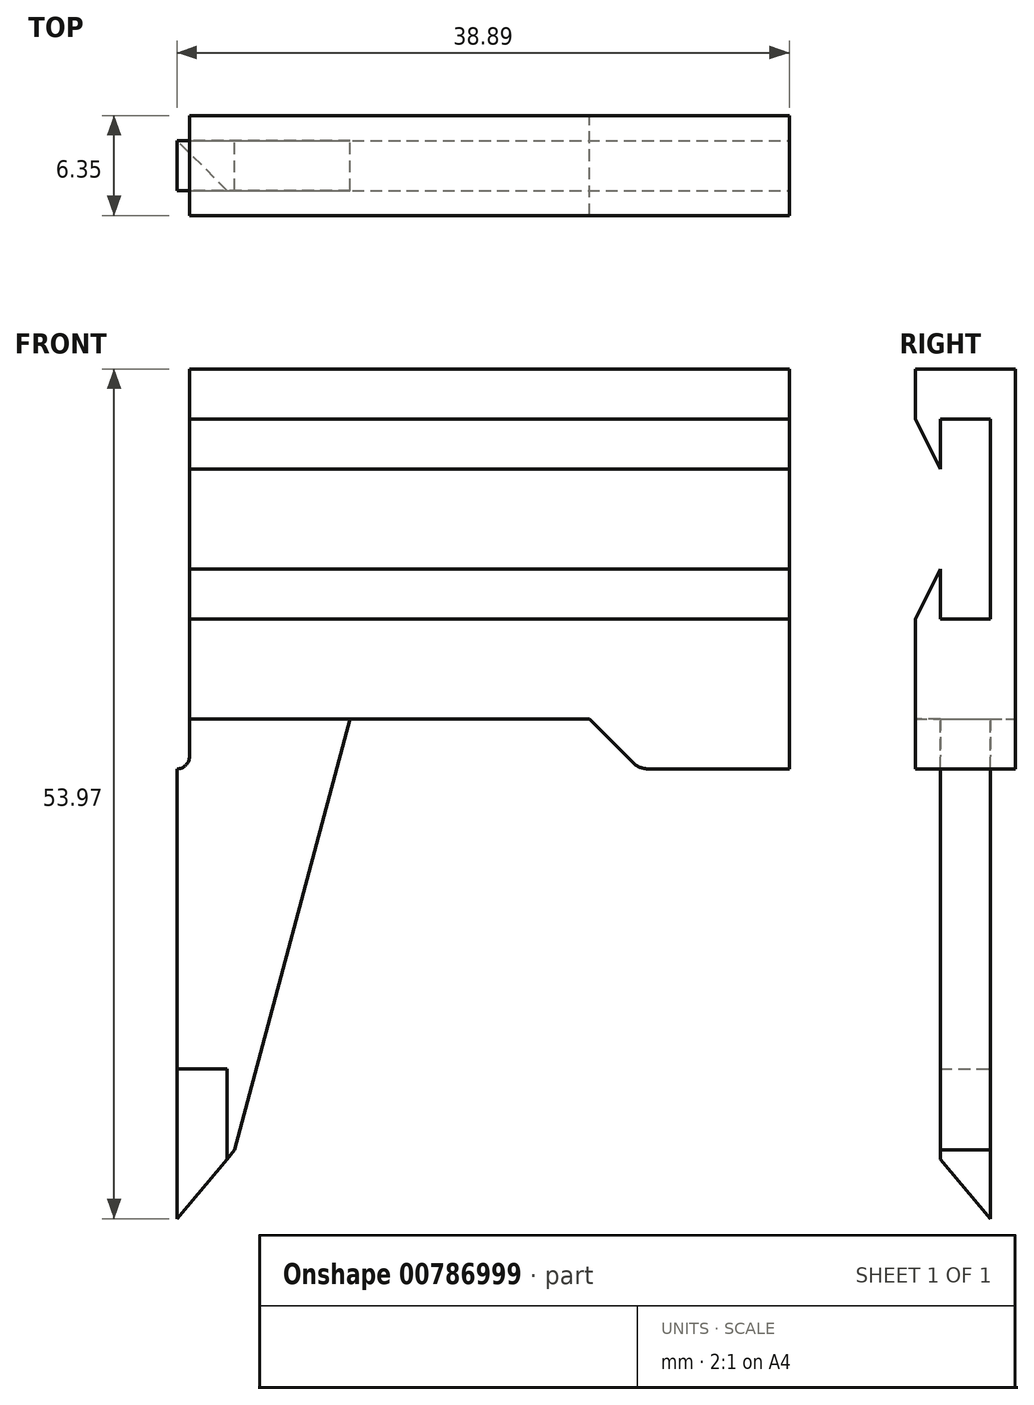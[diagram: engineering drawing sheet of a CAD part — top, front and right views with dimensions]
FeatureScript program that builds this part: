
annotation { "Feature Type Name" : "Feature", "Feature Type Description" : "" }
export const myFeature = defineFeature(function(context is Context, id is Id, definition is map)
    precondition{}
    {
        {
            var Q0;
            Q0=qCreatedBy(makeId("Front.planeOp"),FACE);
            var sketch = newSketch(context, id + "F0", { "sketchPlane" : qUnion([Q0])});
            skLineSegment(sketch, "E0.bottom", {"start": v(19.05, 11.11) * mm, "end": v(-19.05, 11.11) * mm});
            skLineSegment(sketch, "E0.top", {"start": v(6.35, -11.11) * mm, "end": v(-8.84, -11.11) * mm});
            skLineSegment(sketch, "E0.left", {"start": v(19.05, 11.11) * mm, "end": v(19.05, -11.11) * mm});
            skLineSegment(sketch, "E0.right", {"start": v(-19.05, 11.11) * mm, "end": v(-19.05, -11.11) * mm});
            skPoint(sketch, "E0.middle", {"position": v(0, 0) * mm});
            skLineSegment(sketch, "E1", {"start": v(-19.05, -11.11) * mm, "end": v(-19.05, -13.5) * mm});
            skLineSegment(sketch, "E2", {"start": v(6.35, -11.11) * mm, "end": v(9.53, -14.29) * mm});
            skLineSegment(sketch, "E3", {"start": v(9.53, -14.29) * mm, "end": v(19.05, -14.29) * mm});
            skLineSegment(sketch, "E4", {"start": v(19.05, -14.29) * mm, "end": v(19.05, -11.11) * mm});
            skLineSegment(sketch, "E5", {"start": v(-19.84, -14.29) * mm, "end": v(-19.84, -33.34) * mm});
            skLineSegment(sketch, "E6", {"start": v(-16.18, -38.5) * mm, "end": v(-8.84, -11.11) * mm});
            skArc(sketch, "E7", {"start": v(-19.05, -13.5) * mm, "mid": v(-19.28, -14.06) * mm, "end": v(-19.84, -14.29) * mm});
            skLineSegment(sketch, "E8", {"start": v(-19.84, -33.34) * mm, "end": v(-16.66, -33.34) * mm});
            skLineSegment(sketch, "E9", {"start": v(-16.66, -39.08) * mm, "end": v(-16.18, -38.5) * mm});
            skLineSegment(sketch, "E10", {"start": v(-16.66, -33.34) * mm, "end": v(-16.66, -39.08) * mm});
            skPoint(sketch, "E11.orphan", {"position": v(-19.84, -42.86) * mm});
            skSolve(sketch);
        }
        {
            var Q0;
            Q0=makeQuery(id+"F0.imprint","IMPRINT",FACE,{"disambiguationData":[TD([[makeQuery(id+"F0.imprint","IMPRINT",EDGE,{"derivedFrom":sQuery(id+"F0.wireOp",EDGE,"E0.bottom")}),1.0]])]});
            extrude(context, id + "F1", {"entities" : qUnion([Q0]), "depth" : 6.35 * mm, "offsetDistance" : 25.4 * mm});
        }
        {
            var Q0;
            Q0=makeQuery(id+"F1.opExtrude","SWEPT_FACE",FACE,{"disambiguationData":[OSD([sQuery(id+"F0.wireOp",EDGE,"E0.left"),sQuery(id+"F0.wireOp",EDGE,"E4")])]});
            cPlane(context, id + "F2", {"entities" : qUnion([Q0]), "cplaneType" : CPlaneType.OFFSET, "offset" : 0 * mm, "width" : 152.4 * mm, "height" : 152.4 * mm});
        }
        {
            var Q0;
            Q0=qCreatedBy(id+"F2.planeOp",FACE);
            var sketch = newSketch(context, id + "F3", { "sketchPlane" : qUnion([Q0])});
            skLineSegment(sketch, "E12.bottom", {"start": v(-4.76, 7.94) * mm, "end": v(-1.59, 7.94) * mm});
            skLineSegment(sketch, "E12.top", {"start": v(-4.76, -4.76) * mm, "end": v(-1.59, -4.76) * mm});
            skLineSegment(sketch, "E12.right", {"start": v(-1.59, 7.94) * mm, "end": v(-1.59, -4.76) * mm});
            skLineSegment(sketch, "E13", {"start": v(-4.76, 7.94) * mm, "end": v(-4.76, 4.76) * mm});
            skLineSegment(sketch, "E14", {"start": v(-4.76, 4.76) * mm, "end": v(-6.35, 7.94) * mm});
            skLineSegment(sketch, "E15", {"start": v(-6.35, 7.94) * mm, "end": v(-6.35, -4.76) * mm});
            skLineSegment(sketch, "E16", {"start": v(-6.35, -4.76) * mm, "end": v(-4.76, -1.59) * mm});
            skLineSegment(sketch, "E17", {"start": v(-4.76, -1.59) * mm, "end": v(-4.76, -4.76) * mm});
            skSolve(sketch);
        }
        {
            var Q0;
            Q0=makeQuery(id+"F3.imprint","IMPRINT",FACE,{"disambiguationData":[TD([[makeQuery(id+"F3.imprint","IMPRINT",EDGE,{"derivedFrom":sQuery(id+"F3.wireOp",EDGE,"E12.bottom")}),-1.0]])]});
            extrude(context, id + "F4", {"entities" : qUnion([Q0]), "operationType" : NewBodyOperationType.REMOVE, "endBound" : BoundingType.THROUGH_ALL, "oppositeDirection" : true, "depth" : 25.4 * mm, "offsetDistance" : 25.4 * mm});
        }
        {
            var Q0;
            Q0=makeQuery(id+"F1.opExtrude","SWEPT_EDGE",EDGE,{"disambiguationData":[OSD([sQuery(id+"F0.wireOp",EDGE,"E2"),sQuery(id+"F0.wireOp",EDGE,"E3")])]});
            fillet(context, id + "F5", {"entities" : qUnion([Q0]), "radius" : 1.27 * mm, "tangentPropagation" : true, "allowEdgeOverflow" : false});
        }
        {
            var Q0;
            {var subQ0=sQuery(id+"F0.wireOp",EDGE,"E9");var subQ1=sQuery(id+"F0.wireOp",EDGE,"E8");var subQ2=sQuery(id+"F0.wireOp",EDGE,"E7");var subQ3=sQuery(id+"F0.wireOp",EDGE,"E6");var subQ4=sQuery(id+"F0.wireOp",EDGE,"E5");var subQ5=sQuery(id+"F0.wireOp",EDGE,"E3");var subQ6=sQuery(id+"F0.wireOp",EDGE,"E0.top");var subQ7=sQuery(id+"F0.wireOp",EDGE,"E4");var subQ8=sQuery(id+"F0.wireOp",EDGE,"E0.left");var subQ9=sQuery(id+"F0.wireOp",EDGE,"E1");var subQ10=sQuery(id+"F0.wireOp",EDGE,"E0.right");var subQ11=sQuery(id+"F0.wireOp",EDGE,"E2");var subQ12=sQuery(id+"F0.wireOp",EDGE,"E10");Q0=makeQuery(id+"F4.boolean.opBoolean","SPLIT",FACE,{"disambiguationData":[TD([makeQuery(id+"F1.opExtrude","SWEPT_FACE",FACE,{"disambiguationData":[OSD([subQ6])]})])],"derivedFrom":makeQuery(id+"F1.opExtrude","CAP_FACE",FACE,{"disambiguationData":[OSD([sQuery(id+"F0.wireOp",EDGE,"E0.bottom"),subQ6,subQ8,subQ10,subQ9,subQ11,subQ5,subQ7,subQ4,subQ3,subQ2,subQ1,subQ0,subQ12])],"isStart":false})});}
            var sketch = newSketch(context, id + "F6", { "sketchPlane" : qUnion([Q0])});
            skLineSegment(sketch, "E18", {"start": v(-8.84, -11.11) * mm, "end": v(-19.05, -11.11) * mm});
            skSolve(sketch);
        }
        {
            var Q0;
            {var subQ10=sQuery(id+"F6.wireOp",EDGE,"E18");Q0=makeQuery(id+"F6.imprint","IMPRINT",FACE,{"disambiguationData":[TD([[makeQuery(id+"F6.imprint","IMPRINT",EDGE,{"derivedFrom":subQ10}),1.0]])]});}
            extrude(context, id + "F7", {"entities" : qUnion([Q0]), "operationType" : NewBodyOperationType.REMOVE, "oppositeDirection" : true, "depth" : 1.59 * mm, "offsetDistance" : 25.4 * mm});
        }
        {
            var Q0;
            Q0=makeQuery(id+"F1.opExtrude","CAP_FACE",FACE,{"disambiguationData":[OSD([sQuery(id+"F0.wireOp",EDGE,"E0.bottom"),sQuery(id+"F0.wireOp",EDGE,"E0.top"),sQuery(id+"F0.wireOp",EDGE,"E0.left"),sQuery(id+"F0.wireOp",EDGE,"E0.right"),sQuery(id+"F0.wireOp",EDGE,"E1"),sQuery(id+"F0.wireOp",EDGE,"E2"),sQuery(id+"F0.wireOp",EDGE,"E3"),sQuery(id+"F0.wireOp",EDGE,"E4"),sQuery(id+"F0.wireOp",EDGE,"E5"),sQuery(id+"F0.wireOp",EDGE,"E6"),sQuery(id+"F0.wireOp",EDGE,"E7"),sQuery(id+"F0.wireOp",EDGE,"E8"),sQuery(id+"F0.wireOp",EDGE,"E9"),sQuery(id+"F0.wireOp",EDGE,"E10")])],"isStart":true});
            var sketch = newSketch(context, id + "F8", { "sketchPlane" : qUnion([Q0])});
            skLineSegment(sketch, "E19", {"start": v(8.84, -11.11) * mm, "end": v(19.05, -11.11) * mm});
            skSolve(sketch);
        }
        {
            var Q0;
            {var subQ1=sQuery(id+"F8.wireOp",EDGE,"E19");Q0=makeQuery(id+"F8.imprint","IMPRINT",FACE,{"disambiguationData":[TD([[makeQuery(id+"F8.imprint","IMPRINT",EDGE,{"derivedFrom":subQ1}),-1.0]])]});}
            extrude(context, id + "F9", {"entities" : qUnion([Q0]), "operationType" : NewBodyOperationType.REMOVE, "oppositeDirection" : true, "depth" : 1.59 * mm, "offsetDistance" : 25.4 * mm});
        }
        {
            var Q0;
            Q0=makeQuery(id+"F1.opExtrude","SWEPT_FACE",FACE,{"disambiguationData":[OSD([sQuery(id+"F0.wireOp",EDGE,"E8")])]});
            var sketch = newSketch(context, id + "F10", { "sketchPlane" : qUnion([Q0])});
            skLineSegment(sketch, "E20", {"start": v(-16.66, 4.76) * mm, "end": v(-19.84, 1.59) * mm});
            skSolve(sketch);
        }
        {
            var Q0;
            Q0=makeQuery(id+"F10.imprint","IMPRINT",FACE,{"disambiguationData":[TD([[makeQuery(id+"F10.imprint","IMPRINT",EDGE,{"derivedFrom":sQuery(id+"F10.wireOp",EDGE,"E20")}),1.0]])]});
            extrude(context, id + "F11", {"entities" : qUnion([Q0]), "operationType" : NewBodyOperationType.ADD, "depth" : 9.52 * mm, "offsetDistance" : 25.4 * mm});
        }
        {
            var Q0;
            {var subQ0=sQuery(id+"F0.wireOp",EDGE,"E8");Q0=makeQuery(id+"F11.boolean.opBoolean","MERGE",FACE,{"derivedFrom":[makeQuery(id+"F9.boolean.opBoolean","COPY",FACE,{"derivedFrom":makeQuery(id+"F9.opExtrude","CAP_FACE",FACE,{"disambiguationData":[OSD([sQuery(id+"F0.wireOp",EDGE,"E0.right"),sQuery(id+"F0.wireOp",EDGE,"E1"),sQuery(id+"F0.wireOp",EDGE,"E5"),sQuery(id+"F0.wireOp",EDGE,"E6"),sQuery(id+"F0.wireOp",EDGE,"E7"),subQ0,sQuery(id+"F0.wireOp",EDGE,"E9"),sQuery(id+"F0.wireOp",EDGE,"E10"),sQuery(id+"F8.wireOp",EDGE,"E19")])],"isStart":false})}),makeQuery(id+"F11.opExtrude","SWEPT_FACE",FACE,{"disambiguationData":[OSD([subQ0])]})]});}
            var sketch = newSketch(context, id + "F12", { "sketchPlane" : qUnion([Q0])});
            skLineSegment(sketch, "E21", {"start": v(16.66, -39.08) * mm, "end": v(19.84, -42.86) * mm});
            skSolve(sketch);
        }
        {
            var Q0;
            Q0=makeQuery(id+"F12.imprint","IMPRINT",FACE,{"disambiguationData":[TD([[makeQuery(id+"F12.imprint","IMPRINT",EDGE,{"derivedFrom":sQuery(id+"F12.wireOp",EDGE,"E21")}),-1.0]])]});
            extrude(context, id + "F13", {"entities" : qUnion([Q0]), "operationType" : NewBodyOperationType.REMOVE, "endBound" : BoundingType.THROUGH_ALL, "oppositeDirection" : true, "depth" : 25.4 * mm, "offsetDistance" : 25.4 * mm});
        }
    });
